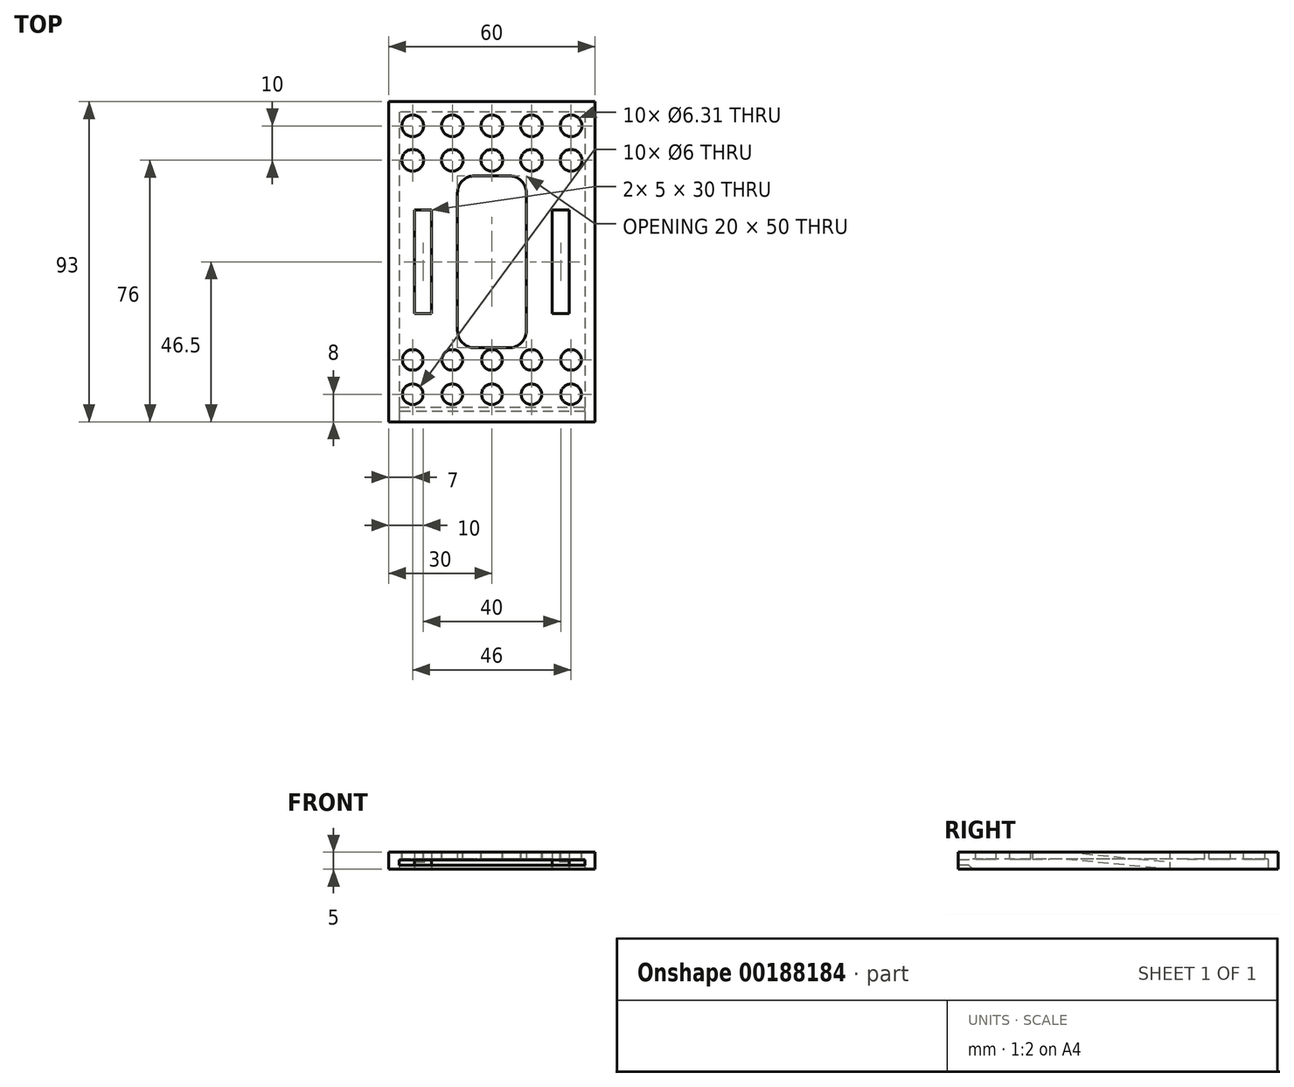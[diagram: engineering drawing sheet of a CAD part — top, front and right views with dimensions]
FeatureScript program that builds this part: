
annotation { "Feature Type Name" : "Feature", "Feature Type Description" : "" }
export const myFeature = defineFeature(function(context is Context, id is Id, definition is map)
    precondition{}
    {
        {
            var Q0;
            Q0=qCreatedBy(makeId("Top.planeOp"),FACE);
            var sketch = newSketch(context, id + "F0", { "sketchPlane" : qUnion([Q0])});
            skLineSegment(sketch, "E0.bottom", {"start": v(27, 43.5) * mm, "end": v(-27, 43.5) * mm});
            skLineSegment(sketch, "E0.top", {"start": v(27, -43.5) * mm, "end": v(-27, -43.5) * mm});
            skLineSegment(sketch, "E0.left", {"start": v(27, 43.5) * mm, "end": v(27, -43.5) * mm});
            skLineSegment(sketch, "E0.right", {"start": v(-27, 43.5) * mm, "end": v(-27, -43.5) * mm});
            skPoint(sketch, "E0.middle", {"position": v(0, 0) * mm});
            skLineSegment(sketch, "E1.bottom", {"start": v(30, 46.5) * mm, "end": v(-30, 46.5) * mm});
            skLineSegment(sketch, "E1.top", {"start": v(30, -46.5) * mm, "end": v(-30, -46.5) * mm});
            skLineSegment(sketch, "E1.left", {"start": v(30, 46.5) * mm, "end": v(30, -46.5) * mm});
            skLineSegment(sketch, "E1.right", {"start": v(-30, 46.5) * mm, "end": v(-30, -46.5) * mm});
            skSolve(sketch);
        }
        {
            var Q0;
            Q0=makeQuery(id+"F0.imprint","IMPRINT",FACE,{"disambiguationData":[TD([[makeQuery(id+"F0.imprint","IMPRINT",EDGE,{"derivedFrom":sQuery(id+"F0.wireOp",EDGE,"E0.bottom")}),-1.0]])]});
            extrude(context, id + "F1", {"entities" : qUnion([Q0]), "depth" : 3 * mm});
        }
        {
            var Q0;
            Q0=makeQuery(id+"F1.opExtrude","CAP_FACE",FACE,{"disambiguationData":[OSD([sQuery(id+"F0.wireOp",EDGE,"E0.bottom"),sQuery(id+"F0.wireOp",EDGE,"E0.top"),sQuery(id+"F0.wireOp",EDGE,"E0.left"),sQuery(id+"F0.wireOp",EDGE,"E0.right"),sQuery(id+"F0.wireOp",EDGE,"E1.bottom"),sQuery(id+"F0.wireOp",EDGE,"E1.top"),sQuery(id+"F0.wireOp",EDGE,"E1.left"),sQuery(id+"F0.wireOp",EDGE,"E1.right")])],"isStart":false});
            var sketch = newSketch(context, id + "F2", { "sketchPlane" : qUnion([Q0])});
            skLineSegment(sketch, "E2.bottom", {"start": v(30, 46.5) * mm, "end": v(-30, 46.5) * mm});
            skLineSegment(sketch, "E2.top", {"start": v(30, -46.5) * mm, "end": v(-30, -46.5) * mm});
            skLineSegment(sketch, "E2.left", {"start": v(30, 46.5) * mm, "end": v(30, -46.5) * mm});
            skLineSegment(sketch, "E2.right", {"start": v(-30, 46.5) * mm, "end": v(-30, -46.5) * mm});
            skPoint(sketch, "E2.middle", {"position": v(0, 0) * mm});
            skLineSegment(sketch, "E3.bottom", {"start": v(5, 25) * mm, "end": v(-5, 25) * mm});
            skLineSegment(sketch, "E3.top", {"start": v(5, -25) * mm, "end": v(-5, -25) * mm});
            skLineSegment(sketch, "E3.left", {"start": v(10, 20) * mm, "end": v(10, -20) * mm});
            skLineSegment(sketch, "E3.right", {"start": v(-10, 20) * mm, "end": v(-10, -20) * mm});
            skPoint(sketch, "E4.visualSharp", {"position": v(-10, 25) * mm});
            skArc(sketch, "E4.filletArc", {"start": v(-5, 25) * mm, "mid": v(-8.54, 23.54) * mm, "end": v(-10, 20) * mm});
            skPoint(sketch, "E5.visualSharp", {"position": v(10, 25) * mm});
            skArc(sketch, "E5.filletArc", {"start": v(10, 20) * mm, "mid": v(8.54, 23.54) * mm, "end": v(5, 25) * mm});
            skPoint(sketch, "E6.visualSharp", {"position": v(10, -25) * mm});
            skArc(sketch, "E6.filletArc", {"start": v(5, -25) * mm, "mid": v(8.54, -23.54) * mm, "end": v(10, -20) * mm});
            skPoint(sketch, "E7.visualSharp", {"position": v(-10, -25) * mm});
            skArc(sketch, "E7.filletArc", {"start": v(-10, -20) * mm, "mid": v(-8.54, -23.54) * mm, "end": v(-5, -25) * mm});
            skLineSegment(sketch, "E8", {"start": v(-30, 0) * mm, "end": v(-20, 0) * mm, "construction": true});
            skPoint(sketch, "E8.endSnap0", {"position": v(-30, 0) * mm});
            skLineSegment(sketch, "E9", {"start": v(30, 0) * mm, "end": v(20, 0) * mm, "construction": true});
            skPoint(sketch, "E9.endSnap0", {"position": v(30, 0) * mm});
            skLineSegment(sketch, "E10.bottom", {"start": v(-17.5, 15) * mm, "end": v(-22.5, 15) * mm});
            skLineSegment(sketch, "E10.top", {"start": v(-17.5, -15) * mm, "end": v(-22.5, -15) * mm});
            skLineSegment(sketch, "E10.left", {"start": v(-17.5, 15) * mm, "end": v(-17.5, -15) * mm});
            skLineSegment(sketch, "E10.right", {"start": v(-22.5, 15) * mm, "end": v(-22.5, -15) * mm});
            skPoint(sketch, "E10.middle", {"position": v(-20, 0) * mm});
            skLineSegment(sketch, "E11.bottom", {"start": v(22.5, 15) * mm, "end": v(17.5, 15) * mm});
            skLineSegment(sketch, "E11.top", {"start": v(22.5, -15) * mm, "end": v(17.5, -15) * mm});
            skLineSegment(sketch, "E11.left", {"start": v(22.5, 15) * mm, "end": v(22.5, -15) * mm});
            skLineSegment(sketch, "E11.right", {"start": v(17.5, 15) * mm, "end": v(17.5, -15) * mm});
            skPoint(sketch, "E11.middle", {"position": v(20, 0) * mm});
            skSolve(sketch);
        }
        {
            var Q0;
            Q0 = qSketchRegion(id + "F2", true);
            extrude(context, id + "F3", {"entities" : qUnion([Q0]), "operationType" : NewBodyOperationType.ADD, "depth" : 2 * mm});
        }
        {
            var Q0;
            Q0=makeQuery(id+"F3.opExtrude","SWEPT_FACE",FACE,{"disambiguationData":[OSD([sQuery(id+"F2.wireOp",EDGE,"E10.left")])]});
            var sketch = newSketch(context, id + "F4", { "sketchPlane" : qUnion([Q0])});
            skLineSegment(sketch, "E12", {"start": v(15, 5) * mm, "end": v(-15, 2.11) * mm});
            skLineSegment(sketch, "E13", {"start": v(15, 3) * mm, "end": v(-15, 0.11) * mm});
            skLineSegment(sketch, "E14", {"start": v(-15, 2.11) * mm, "end": v(-15, 0.11) * mm});
            skLineSegment(sketch, "E15", {"start": v(15, 3) * mm, "end": v(15, 5) * mm});
            skSolve(sketch);
        }
        {
            var Q0;
            Q0 = qSketchRegion(id + "F4", true);
            extrude(context, id + "F5", {"entities" : qUnion([Q0]), "operationType" : NewBodyOperationType.ADD, "depth" : 5 * mm});
        }
        {
            var Q0;
            Q0=makeQuery(id+"F3.opExtrude","SWEPT_FACE",FACE,{"disambiguationData":[OSD([sQuery(id+"F2.wireOp",EDGE,"E11.right")])]});
            var sketch = newSketch(context, id + "F6", { "sketchPlane" : qUnion([Q0])});
            skLineSegment(sketch, "E16", {"start": v(-15, 5) * mm, "end": v(15, 2.11) * mm});
            skLineSegment(sketch, "E17", {"start": v(15, 2.11) * mm, "end": v(15, 0.11) * mm});
            skLineSegment(sketch, "E18", {"start": v(15, 0.11) * mm, "end": v(-15, 3) * mm});
            skLineSegment(sketch, "E19", {"start": v(-15, 3) * mm, "end": v(-15, 5) * mm});
            skSolve(sketch);
        }
        {
            var Q0;
            Q0 = qSketchRegion(id + "F6", true);
            extrude(context, id + "F7", {"entities" : qUnion([Q0]), "operationType" : NewBodyOperationType.ADD, "depth" : 5 * mm});
        }
        {
            var Q0;
            Q0=makeQuery(id+"F3.boolean.opBoolean","MERGE",FACE,{"derivedFrom":[makeQuery(id+"F1.opExtrude","SWEPT_FACE",FACE,{"disambiguationData":[OSD([sQuery(id+"F0.wireOp",EDGE,"E1.top")])]}),makeQuery(id+"F3.opExtrude","SWEPT_FACE",FACE,{"disambiguationData":[OSD([sQuery(id+"F2.wireOp",EDGE,"E2.top")])]})]});
            var sketch = newSketch(context, id + "F8", { "sketchPlane" : qUnion([Q0])});
            skLineSegment(sketch, "E20", {"start": v(0, 0) * mm, "end": v(0, 2) * mm, "construction": true});
            skLineSegment(sketch, "E21.bottom", {"start": v(27, 2.75) * mm, "end": v(-27, 2.75) * mm});
            skLineSegment(sketch, "E21.top", {"start": v(27, 1.25) * mm, "end": v(-27, 1.25) * mm});
            skLineSegment(sketch, "E21.left", {"start": v(27, 2.75) * mm, "end": v(27, 1.25) * mm});
            skLineSegment(sketch, "E21.right", {"start": v(-27, 2.75) * mm, "end": v(-27, 1.25) * mm});
            skPoint(sketch, "E21.middle", {"position": v(0, 2) * mm});
            skSolve(sketch);
        }
        {
            var Q0;
            Q0 = qSketchRegion(id + "F8", true);
            extrude(context, id + "F9", {"entities" : qUnion([Q0]), "operationType" : NewBodyOperationType.REMOVE, "oppositeDirection" : true, "depth" : 5 * mm});
        }
        {
            var Q0;
            Q0=makeQuery(id+"F9.boolean.opBoolean","MERGE",FACE,{"derivedFrom":[makeQuery(id+"F1.opExtrude","SWEPT_FACE",FACE,{"disambiguationData":[OSD([sQuery(id+"F0.wireOp",EDGE,"E0.left")])]}),makeQuery(id+"F9.opExtrude","SWEPT_FACE",FACE,{"disambiguationData":[OSD([sQuery(id+"F8.wireOp",EDGE,"E21.left")])]})]});
            var sketch = newSketch(context, id + "F10", { "sketchPlane" : qUnion([Q0])});
            skLineSegment(sketch, "E22", {"start": v(43.5, 1.25) * mm, "end": v(43.5, 0) * mm});
            skLineSegment(sketch, "E23", {"start": v(43.5, 0) * mm, "end": v(42.25, 0) * mm});
            skLineSegment(sketch, "E24", {"start": v(43.5, 1.25) * mm, "end": v(42.25, 0) * mm});
            skSolve(sketch);
        }
        {
            var Q0;
            Q0=makeQuery(id+"F10.imprint","IMPRINT",FACE,{"disambiguationData":[TD([[makeQuery(id+"F10.imprint","IMPRINT",EDGE,{"derivedFrom":sQuery(id+"F10.wireOp",EDGE,"E22")}),-1.0]])]});
            extrude(context, id + "F11", {"entities" : qUnion([Q0]), "operationType" : NewBodyOperationType.ADD, "endBound" : BoundingType.UP_TO_NEXT, "depth" : 25 * mm});
        }
        {
            var Q0;
            Q0=makeQuery(id+"F3.opExtrude","CAP_FACE",FACE,{"disambiguationData":[OSD([sQuery(id+"F2.wireOp",EDGE,"E2.bottom"),sQuery(id+"F2.wireOp",EDGE,"E2.top"),sQuery(id+"F2.wireOp",EDGE,"E2.left"),sQuery(id+"F2.wireOp",EDGE,"E2.right"),sQuery(id+"F2.wireOp",EDGE,"E3.bottom"),sQuery(id+"F2.wireOp",EDGE,"E3.top"),sQuery(id+"F2.wireOp",EDGE,"E3.left"),sQuery(id+"F2.wireOp",EDGE,"E3.right"),sQuery(id+"F2.wireOp",EDGE,"E4.filletArc"),sQuery(id+"F2.wireOp",EDGE,"E5.filletArc"),sQuery(id+"F2.wireOp",EDGE,"E6.filletArc"),sQuery(id+"F2.wireOp",EDGE,"E7.filletArc"),sQuery(id+"F2.wireOp",EDGE,"E10.bottom"),sQuery(id+"F2.wireOp",EDGE,"E10.top"),sQuery(id+"F2.wireOp",EDGE,"E10.left"),sQuery(id+"F2.wireOp",EDGE,"E10.right"),sQuery(id+"F2.wireOp",EDGE,"E11.bottom"),sQuery(id+"F2.wireOp",EDGE,"E11.top"),sQuery(id+"F2.wireOp",EDGE,"E11.left"),sQuery(id+"F2.wireOp",EDGE,"E11.right")])],"isStart":false});
            var sketch = newSketch(context, id + "F12", { "sketchPlane" : qUnion([Q0])});
            skCircle(sketch, "E25", {"center": v(-23, 39.5) * mm, "radius": 3.15 * mm});
            skCircle(sketch, "E26.0.1.0", {"center": v(-23, 29.5) * mm, "radius": 3.15 * mm});
            skCircle(sketch, "E26.1.0.0", {"center": v(-11.5, 39.5) * mm, "radius": 3.15 * mm});
            skCircle(sketch, "E26.1.1.0", {"center": v(-11.5, 29.5) * mm, "radius": 3.15 * mm});
            skCircle(sketch, "E26.2.0.0", {"center": v(0, 39.5) * mm, "radius": 3.15 * mm});
            skCircle(sketch, "E26.2.1.0", {"center": v(0, 29.5) * mm, "radius": 3.15 * mm});
            skCircle(sketch, "E26.3.0.0", {"center": v(11.5, 39.5) * mm, "radius": 3.15 * mm});
            skCircle(sketch, "E26.3.1.0", {"center": v(11.5, 29.5) * mm, "radius": 3.15 * mm});
            skCircle(sketch, "E26.4.0.0", {"center": v(23, 39.5) * mm, "radius": 3.15 * mm});
            skCircle(sketch, "E26.4.1.0", {"center": v(23, 29.5) * mm, "radius": 3.15 * mm});
            skLineSegment(sketch, "E26.direction1", {"start": v(-23, 39.5) * mm, "end": v(-11.5, 39.5) * mm, "construction": true});
            skLineSegment(sketch, "E26.direction2", {"start": v(-23, 39.5) * mm, "end": v(-23, 29.5) * mm, "construction": true});
            skCircle(sketch, "E27", {"center": v(-23, -38.5) * mm, "radius": 3 * mm});
            skCircle(sketch, "E28.0.1.0", {"center": v(-23, -28.5) * mm, "radius": 3 * mm});
            skCircle(sketch, "E28.1.0.0", {"center": v(-11.5, -38.5) * mm, "radius": 3 * mm});
            skCircle(sketch, "E28.1.1.0", {"center": v(-11.5, -28.5) * mm, "radius": 3 * mm});
            skCircle(sketch, "E28.2.0.0", {"center": v(0, -38.5) * mm, "radius": 3 * mm});
            skCircle(sketch, "E28.2.1.0", {"center": v(0, -28.5) * mm, "radius": 3 * mm});
            skCircle(sketch, "E28.3.0.0", {"center": v(11.5, -38.5) * mm, "radius": 3 * mm});
            skCircle(sketch, "E28.3.1.0", {"center": v(11.5, -28.5) * mm, "radius": 3 * mm});
            skCircle(sketch, "E28.4.0.0", {"center": v(23, -38.5) * mm, "radius": 3 * mm});
            skCircle(sketch, "E28.4.1.0", {"center": v(23, -28.5) * mm, "radius": 3 * mm});
            skLineSegment(sketch, "E28.direction1", {"start": v(-23, -38.5) * mm, "end": v(-11.5, -38.5) * mm, "construction": true});
            skLineSegment(sketch, "E28.direction2", {"start": v(-23, -38.5) * mm, "end": v(-23, -28.5) * mm, "construction": true});
            skSolve(sketch);
        }
        {
            var Q0;
            Q0 = qSketchRegion(id + "F12", true);
            extrude(context, id + "F13", {"entities" : qUnion([Q0]), "operationType" : NewBodyOperationType.REMOVE, "oppositeDirection" : true, "depth" : 25 * mm});
        }
    });
